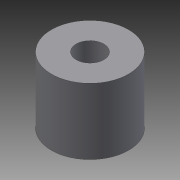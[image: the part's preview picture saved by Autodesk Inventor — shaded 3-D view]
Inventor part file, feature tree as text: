
AUTODESK INVENTOR PART (.ipt)
format: ipt  version: 2014 (Build 180170000, 170)  size: 72,704 bytes
history: native  units: mm
features: other x1, extrude x1, sketch x1
ambient origin geometry x8: Origin, YZ Plane, XZ Plane, XY Plane, X Axis, Y Axis, Z Axis, Center Point
bodies: Body1 (feature_tree)
feature tree (3):
  other  "Твердое тело1"
  extrude  "Выдавливание1"  Depth=2.5mm
  sketch  "Эскиз1"
